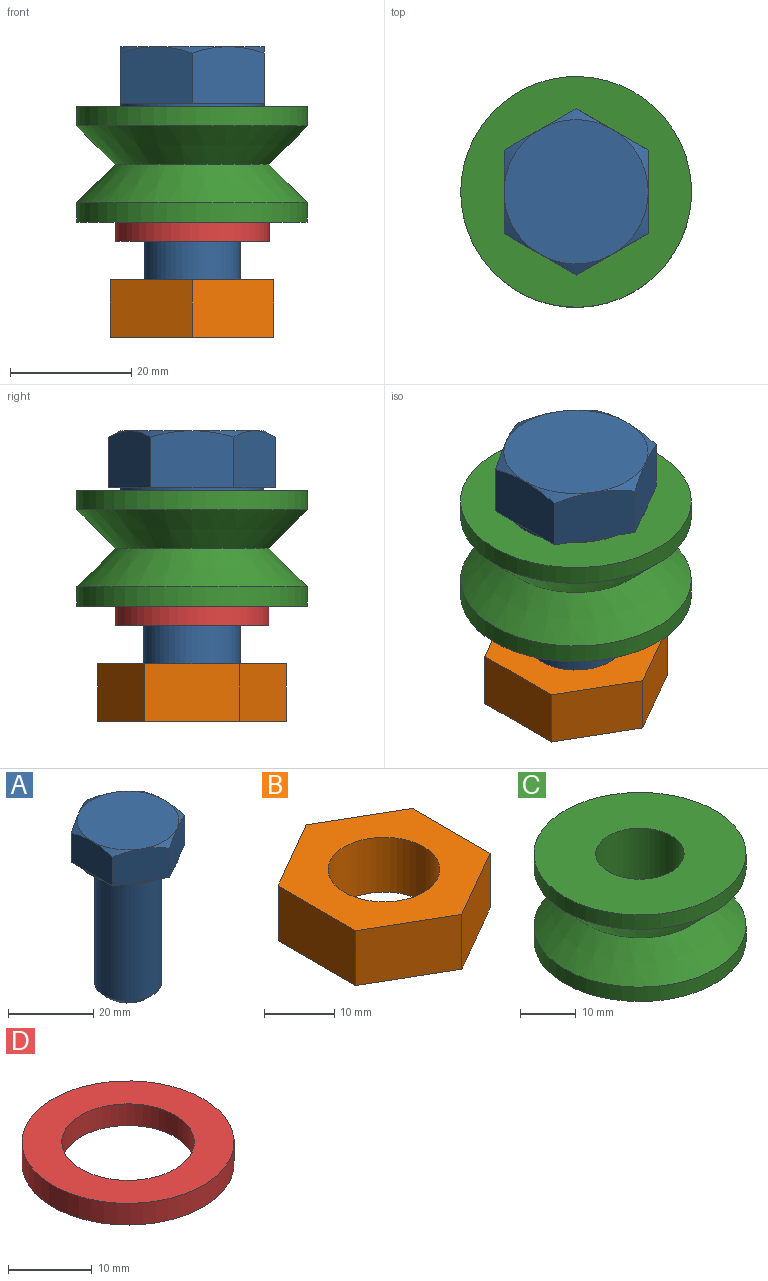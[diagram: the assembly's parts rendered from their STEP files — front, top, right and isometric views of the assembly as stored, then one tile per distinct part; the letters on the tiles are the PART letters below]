
ASSEMBLY  parts=4 mates=3
PART A: 25 faces, bbox 27.5x27.5x48 mm
  f0: plane 10.31x5.95mm, normal (0,0,-1), area 7.6mm2, adj f6,f12,f17
  f1: plane 10.31x5.95mm, normal (0,0,-1), area 7.6mm2, adj f6,f12,f13
  f2: plane 11.91x3.44mm, normal (0,0,-1), area 7.6mm2, adj f6,f13,f14
  f3: plane 10.31x5.95mm, normal (0,0,-1), area 7.6mm2, adj f6,f14,f15
  f4: plane 10.31x5.95mm, normal (0,0,-1), area 7.6mm2, adj f6,f15,f16
  f5: plane 11.91x3.44mm, normal (0,0,-1), area 7.6mm2, adj f6,f16,f17
  f6: cylinder r=11.91mm len=23.81mm, axis (0,0,-1), area 38mm2, adj f0,f1,f2,f3,f4,f5,f7
  f7: plane 23.81x23.81mm, normal (0,0,-1), area 204.1mm2, adj f6,f8
  f8: torus R=8.76mm, axis (0,0,-1), area 67.1mm2, adj f7,f9
  f9: cylinder r=7.94mm len=35.43mm, axis (0,0,-1), area 1767.1mm2, adj f8,f10
  f10: cone r=7.94mm half-angle=45deg, axis (0,0,1), area 114.8mm2, adj f9,f11
  f11: plane 12.19x12.19mm, normal (0,0,-1), area 116.7mm2, adj f10
  f12: plane 13.76x9.42mm, normal (-1,0,0), area 124.4mm2, adj f0,f1,f13,f17,f20,f21
  f13: plane 11.91x9.42mm, normal (-0.5,0.87,0), area 124.4mm2, adj f1,f2,f12,f14,f21,f22
  f14: plane 11.91x9.42mm, normal (0.5,0.87,0), area 124.4mm2, adj f2,f3,f13,f15,f18,f22
  f15: plane 13.76x9.42mm, normal (1,0,0), area 124.4mm2, adj f3,f4,f14,f16,f18,f19
  f16: plane 11.91x9.42mm, normal (0.5,-0.87,0), area 124.4mm2, adj f4,f5,f15,f17,f19,f24
  f17: plane 11.91x9.42mm, normal (-0.5,-0.87,0), area 124.4mm2, adj f0,f5,f12,f16,f20,f24
  f18: cone r=11.91mm half-angle=60deg, axis (0,0,-1), area 8.8mm2, adj f14,f15,f23
  f19: cone r=11.91mm half-angle=60deg, axis (0,0,-1), area 8.8mm2, adj f15,f16,f23
  f20: cone r=11.91mm half-angle=60deg, axis (0,0,-1), area 8.8mm2, adj f12,f17,f23
  f21: cone r=11.91mm half-angle=60deg, axis (0,0,-1), area 8.8mm2, adj f12,f13,f23
  f22: cone r=11.91mm half-angle=60deg, axis (0,0,-1), area 8.8mm2, adj f13,f14,f23
  f23: plane 23.81x23.81mm, normal (0,0,1), area 445.3mm2, adj f18,f19,f20,f21,f22,f24
  f24: cone r=11.91mm half-angle=60deg, axis (0,0,-1), area 8.8mm2, adj f16,f17,f23
PART B: 9 faces, bbox 27x31.2x9.5 mm
  f0: plane 13.49x9.53mm, normal (0.5,-0.87,0), area 148.4mm2, adj f1,f6,f7,f8
  f1: plane 15.58x9.53mm, normal (1,0,0), area 148.4mm2, adj f0,f2,f7,f8
  f2: plane 13.49x9.53mm, normal (0.5,0.87,0), area 148.4mm2, adj f1,f3,f7,f8
  f3: plane 13.49x9.53mm, normal (-0.5,0.87,0), area 148.4mm2, adj f2,f4,f7,f8
  f4: plane 15.58x9.53mm, normal (-1,0,0), area 148.4mm2, adj f3,f6,f7,f8
  f5: cylinder r=7.94mm len=15.88mm, axis (0,0,-1), area 475mm2, adj f7,f8
  f6: plane 13.49x9.53mm, normal (-0.5,-0.87,0), area 148.4mm2, adj f0,f4,f7,f8
  f7: plane 31.16x26.99mm, normal (0,0,1), area 432.8mm2, adj f0,f1,f2,f3,f4,f5,f6
  f8: plane 31.16x26.99mm, normal (0,0,-1), area 432.8mm2, adj f0,f1,f2,f3,f4,f5,f6
PART C: 7 faces, bbox 38.1x38.1x19.1 mm
  f0: cylinder r=7.94mm len=19.05mm, axis (0,0,-1), area 950.1mm2, adj f1,f6
  f1: plane 38.1x38.1mm, normal (0,0,1), area 942.2mm2, adj f0,f2
  f2: cylinder r=19.05mm len=38.1mm, axis (0,0,-1), area 380mm2, adj f1,f3
  f3: cone r=12.7mm half-angle=45deg, axis (0,0,1), area 895.7mm2, adj f2,f4
  f4: cone r=19.05mm half-angle=45deg, axis (0,0,-1), area 895.7mm2, adj f3,f5
  f5: cylinder r=19.05mm len=38.1mm, axis (0,0,-1), area 380mm2, adj f4,f6
  f6: plane 38.1x38.1mm, normal (0,0,-1), area 942.2mm2, adj f0,f5
PART D: 4 faces, bbox 25.4x25.4x3.2 mm
  f0: cylinder r=7.94mm len=15.88mm, axis (0,0,-1), area 158.3mm2, adj f2,f3
  f1: cylinder r=12.7mm len=25.4mm, axis (0,0,-1), area 253.4mm2, adj f2,f3
  f2: plane 25.4x25.4mm, normal (0,0,1), area 308.8mm2, adj f0,f1
  f3: plane 25.4x25.4mm, normal (0,0,-1), area 308.8mm2, adj f0,f1
PLACE A at identity fixed
PLACE B t=(0,0,-41.28)mm
PLACE C at identity
PLACE D t=(0,0,-22.23)mm
MATE fastened B.f5 <-> D.f1  axis (0,0,1) through (0,0,-28.58)mm
MATE fastened D.f1 <-> C.f0  axis (0,0,1) through (0,0,-19.05)mm
MATE fastened C.f0 <-> A.f6  axis (0,0,1) through (0,0,0)mm
